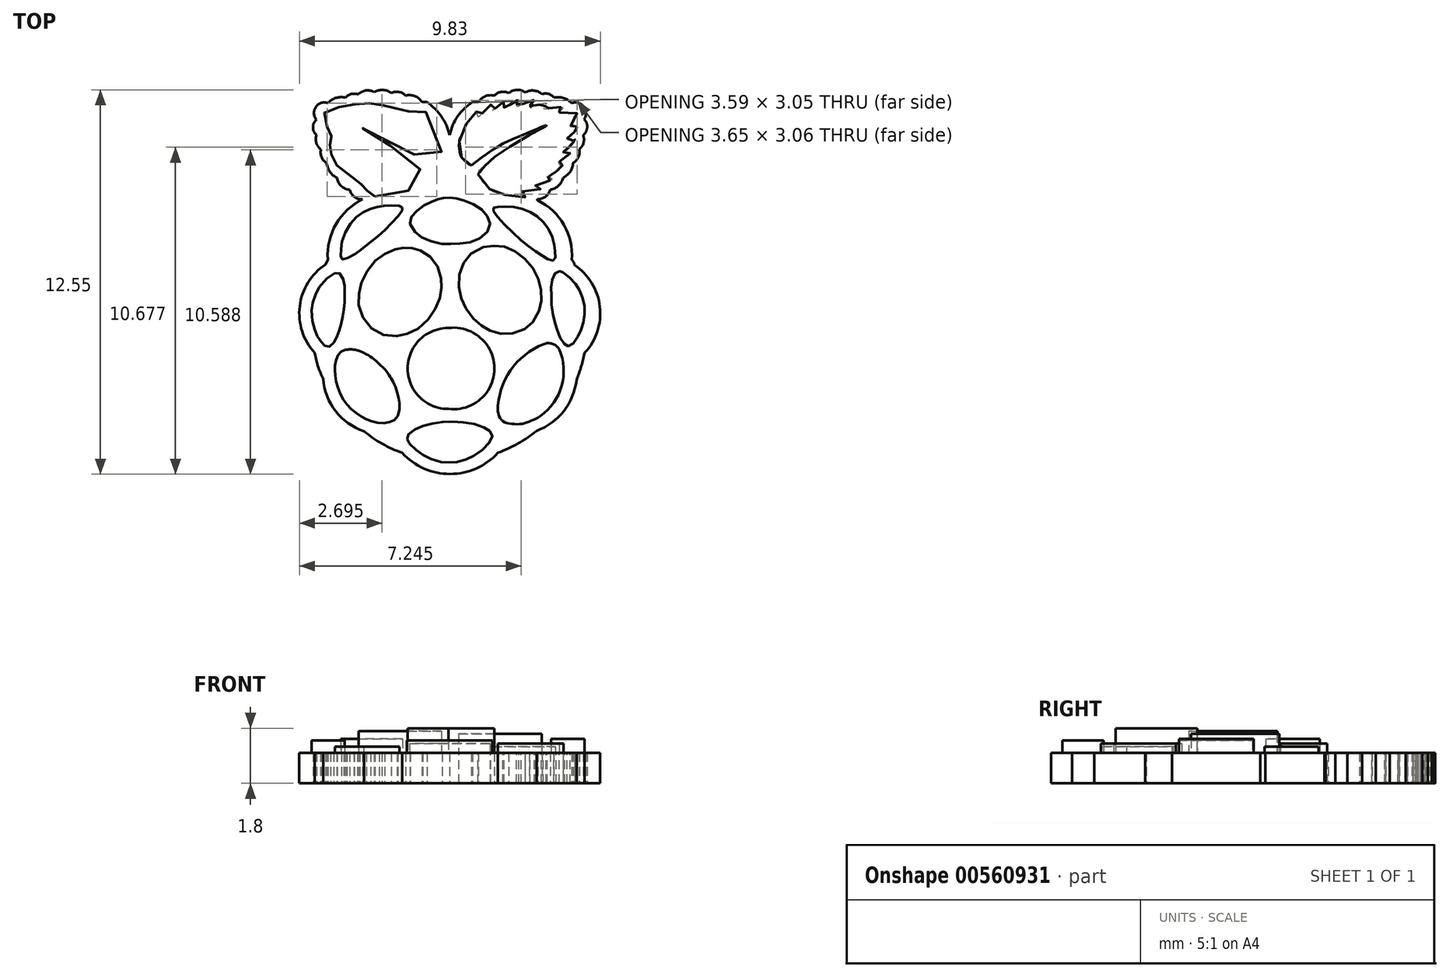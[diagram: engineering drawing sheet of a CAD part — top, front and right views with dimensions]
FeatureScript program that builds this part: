
annotation { "Feature Type Name" : "Feature", "Feature Type Description" : "" }
export const myFeature = defineFeature(function(context is Context, id is Id, definition is map)
    precondition{}
    {
        {
            var Q0;
            Q0=qCreatedBy(makeId("Top.planeOp"),FACE);
            var sketch = newSketch(context, id + "F0", { "sketchPlane" : qUnion([Q0])});
            skPoint(sketch, "E0", {"position": v(-4.99, 0) * mm});
            skArc(sketch, "E1", {"start": v(-2.8, 2.9) * mm, "mid": v(-3.67, 2.1) * mm, "end": v(-3.94, 0.95) * mm});
            skFitSpline(sketch, "E2", {"points": [v(-3.94, 0.95) * mm, v(-4.02, 0.78) * mm], "startDerivative": vector(-0.08, -0.17) * mm, "endDerivative": vector(-0.08, -0.17) * mm});
            skArc(sketch, "E3", {"start": v(-4.02, 0.78) * mm, "mid": v(-4.86, -0.59) * mm, "end": v(-4.37, -2.11) * mm});
            skArc(sketch, "E4", {"start": v(-4.37, -2.11) * mm, "mid": v(-4.26, -2.54) * mm, "end": v(-4.1, -2.96) * mm});
            skArc(sketch, "E5", {"start": v(-4.1, -2.96) * mm, "mid": v(-3.69, -4.01) * mm, "end": v(-2.76, -4.67) * mm});
            skArc(sketch, "E6", {"start": v(-2.76, -4.67) * mm, "mid": v(-2.17, -5.08) * mm, "end": v(-1.51, -5.37) * mm});
            skArc(sketch, "E7", {"start": v(-1.51, -5.37) * mm, "mid": v(0.05, -6.07) * mm, "end": v(1.6, -5.37) * mm});
            skArc(sketch, "E8", {"start": v(1.6, -5.37) * mm, "mid": v(2.27, -5.07) * mm, "end": v(2.88, -4.66) * mm});
            skArc(sketch, "E9", {"start": v(2.88, -4.66) * mm, "mid": v(3.76, -4) * mm, "end": v(4.18, -2.99) * mm});
            skArc(sketch, "E10", {"start": v(4.18, -2.99) * mm, "mid": v(4.33, -2.56) * mm, "end": v(4.45, -2.11) * mm});
            skArc(sketch, "E11", {"start": v(4.45, -2.11) * mm, "mid": v(4.94, -0.6) * mm, "end": v(4.11, 0.76) * mm});
            skArc(sketch, "E12", {"start": v(4.11, 0.76) * mm, "mid": v(4.09, 0.86) * mm, "end": v(4.03, 0.93) * mm});
            skArc(sketch, "E13", {"start": v(4.03, 0.93) * mm, "mid": v(3.77, 2.07) * mm, "end": v(2.92, 2.87) * mm});
            skArc(sketch, "E14", {"start": v(-3.23, 3.22) * mm, "mid": v(-3.07, 2.99) * mm, "end": v(-2.8, 2.9) * mm});
            skArc(sketch, "E15", {"start": v(-3.64, 3.6) * mm, "mid": v(-3.5, 3.34) * mm, "end": v(-3.23, 3.22) * mm});
            skArc(sketch, "E16", {"start": v(-3.98, 4.09) * mm, "mid": v(-3.87, 3.8) * mm, "end": v(-3.64, 3.6) * mm});
            skArc(sketch, "E17", {"start": v(-4.16, 4.53) * mm, "mid": v(-4.15, 4.28) * mm, "end": v(-3.98, 4.09) * mm});
            skArc(sketch, "E18", {"start": v(-4.31, 5) * mm, "mid": v(-4.31, 4.74) * mm, "end": v(-4.16, 4.53) * mm});
            skArc(sketch, "E19", {"start": v(-4.31, 5.5) * mm, "mid": v(-4.43, 5.26) * mm, "end": v(-4.31, 5) * mm});
            skArc(sketch, "E20", {"start": v(-3.94, 6.05) * mm, "mid": v(-4.33, 5.92) * mm, "end": v(-4.31, 5.5) * mm});
            skArc(sketch, "E21", {"start": v(-3.37, 6.23) * mm, "mid": v(-3.68, 6.22) * mm, "end": v(-3.94, 6.05) * mm});
            skArc(sketch, "E22", {"start": v(-2.95, 6.34) * mm, "mid": v(-3.17, 6.35) * mm, "end": v(-3.37, 6.23) * mm});
            skArc(sketch, "E23", {"start": v(-2.43, 6.4) * mm, "mid": v(-2.7, 6.46) * mm, "end": v(-2.95, 6.34) * mm});
            skArc(sketch, "E24", {"start": v(-1.87, 6.38) * mm, "mid": v(-2.15, 6.48) * mm, "end": v(-2.43, 6.4) * mm});
            skArc(sketch, "E25", {"start": v(-1.4, 6.3) * mm, "mid": v(-1.62, 6.41) * mm, "end": v(-1.87, 6.38) * mm});
            skArc(sketch, "E26", {"start": v(-0.87, 6.08) * mm, "mid": v(-1.1, 6.28) * mm, "end": v(-1.4, 6.3) * mm});
            skLineSegment(sketch, "E27", {"start": v(-0.87, 6.08) * mm, "end": v(-0.7, 6.08) * mm});
            skArc(sketch, "E28", {"start": v(0.04, 5) * mm, "mid": v(-0.24, 5.61) * mm, "end": v(-0.7, 6.08) * mm});
            skArc(sketch, "E29", {"start": v(0.79, 6.08) * mm, "mid": v(0.3, 5.62) * mm, "end": v(0.04, 5) * mm});
            skLineSegment(sketch, "E30", {"start": v(0.79, 6.08) * mm, "end": v(0.98, 6.08) * mm});
            skArc(sketch, "E31", {"start": v(1.5, 6.3) * mm, "mid": v(1.2, 6.27) * mm, "end": v(0.98, 6.08) * mm});
            skArc(sketch, "E32", {"start": v(1.97, 6.38) * mm, "mid": v(1.72, 6.41) * mm, "end": v(1.5, 6.3) * mm});
            skArc(sketch, "E33", {"start": v(2.5, 6.4) * mm, "mid": v(2.23, 6.48) * mm, "end": v(1.97, 6.38) * mm});
            skArc(sketch, "E34", {"start": v(3.05, 6.34) * mm, "mid": v(2.79, 6.46) * mm, "end": v(2.5, 6.4) * mm});
            skArc(sketch, "E35", {"start": v(3.44, 6.23) * mm, "mid": v(3.27, 6.35) * mm, "end": v(3.05, 6.34) * mm});
            skArc(sketch, "E36", {"start": v(4.02, 6.05) * mm, "mid": v(3.76, 6.21) * mm, "end": v(3.44, 6.23) * mm});
            skArc(sketch, "E37", {"start": v(4.43, 5.52) * mm, "mid": v(4.42, 5.93) * mm, "end": v(4.02, 6.05) * mm});
            skArc(sketch, "E38", {"start": v(4.4, 5) * mm, "mid": v(4.53, 5.26) * mm, "end": v(4.43, 5.52) * mm});
            skArc(sketch, "E39", {"start": v(4.27, 4.54) * mm, "mid": v(4.4, 4.75) * mm, "end": v(4.4, 5) * mm});
            skArc(sketch, "E40", {"start": v(4.07, 4.1) * mm, "mid": v(4.24, 4.28) * mm, "end": v(4.27, 4.54) * mm});
            skArc(sketch, "E41", {"start": v(3.74, 3.6) * mm, "mid": v(3.97, 3.8) * mm, "end": v(4.07, 4.1) * mm});
            skArc(sketch, "E42", {"start": v(3.33, 3.23) * mm, "mid": v(3.6, 3.35) * mm, "end": v(3.74, 3.6) * mm});
            skArc(sketch, "E43", {"start": v(2.9, 2.9) * mm, "mid": v(3.17, 3) * mm, "end": v(3.33, 3.23) * mm});
            skFitSpline(sketch, "E44", {"points": [v(2.9, 2.9) * mm, v(2.9, 2.9) * mm, v(2.9, 2.88) * mm, v(2.92, 2.87) * mm], "startDerivative": vector(-0.04, -0.02) * mm, "endDerivative": vector(0.06, -0.02) * mm});
            skFitSpline(sketch, "E45", {"points": [v(-1.35, -4.93) * mm, v(-1.36, -4.9) * mm, v(-1.31, -4.78) * mm, v(-1.15, -4.63) * mm, v(-0.91, -4.53) * mm, v(-0.63, -4.44) * mm, v(-0.28, -4.37) * mm, v(0.05, -4.36) * mm, v(0.44, -4.37) * mm, v(0.85, -4.44) * mm, v(1.17, -4.55) * mm, v(1.3, -4.64) * mm, v(1.4, -4.72) * mm, v(1.43, -4.83) * mm, v(1.38, -4.96) * mm, v(1.2, -5.2) * mm, v(0.87, -5.44) * mm, v(0.68, -5.54) * mm, v(0.41, -5.65) * mm, v(0.14, -5.68) * mm, v(-0.01, -5.7) * mm, v(-0.28, -5.67) * mm, v(-0.63, -5.55) * mm, v(-0.83, -5.44) * mm, v(-1.03, -5.3) * mm, v(-1.25, -5.1) * mm, v(-1.32, -5) * mm, v(-1.35, -4.93) * mm]});
            skArc(sketch, "E46", {"start": v(0, -1.3) * mm, "mid": v(-1.33, -2.62) * mm, "end": v(0, -3.94) * mm});
            skArc(sketch, "E47", {"start": v(0, -3.94) * mm, "mid": v(1.5, -2.62) * mm, "end": v(0, -1.3) * mm});
            skLineSegment(sketch, "E48", {"start": v(0.05, -3.96) * mm, "end": v(0.05, -4.44) * mm, "construction": true});
            skLineSegment(sketch, "E49", {"start": v(-4.7, 0) * mm, "end": v(-4.99, 0) * mm, "construction": true});
            skLineSegment(sketch, "E50", {"start": v(0.04, 5) * mm, "end": v(0.05, 6.52) * mm, "construction": true});
            skFitSpline(sketch, "E51", {"points": [v(-3.5, -2.07) * mm, v(-3.4, -2.02) * mm, v(-3.26, -2) * mm, v(-3.14, -2) * mm, v(-3, -2.02) * mm, v(-2.88, -2.06) * mm, v(-2.77, -2.11) * mm], "startDerivative": vector(0.63, 0.36) * mm, "endDerivative": vector(0.7, -0.31) * mm});
            skFitSpline(sketch, "E52", {"points": [v(-2.77, -2.11) * mm, v(-2.6, -2.2) * mm, v(-2.46, -2.3) * mm, v(-2.3, -2.44) * mm, v(-2.05, -2.69) * mm, v(-1.92, -2.88) * mm, v(-1.86, -2.95) * mm, v(-1.78, -3.12) * mm, v(-1.7, -3.34) * mm, v(-1.64, -3.53) * mm, v(-1.62, -3.6) * mm], "startDerivative": vector(2.02, -1.01) * mm, "endDerivative": vector(0.5, -0.89) * mm});
            skFitSpline(sketch, "E53", {"points": [v(-1.62, -3.6) * mm, v(-1.6, -3.74) * mm, v(-1.6, -3.98) * mm, v(-1.7, -4.24) * mm, v(-1.83, -4.34) * mm, v(-2.03, -4.4) * mm, v(-2.27, -4.4) * mm, v(-2.54, -4.34) * mm, v(-2.7, -4.27) * mm, v(-2.9, -4.16) * mm, v(-3.1, -4) * mm, v(-3.3, -3.82) * mm, v(-3.43, -3.64) * mm, v(-3.56, -3.38) * mm, v(-3.66, -3.1) * mm, v(-3.7, -2.84) * mm, v(-3.71, -2.68) * mm, v(-3.71, -2.54) * mm, v(-3.67, -2.33) * mm, v(-3.6, -2.16) * mm, v(-3.5, -2.07) * mm], "startDerivative": vector(0.52, -3.3) * mm, "endDerivative": vector(2.4, 2.14) * mm});
            skArc(sketch, "E54", {"start": v(3.1, -1.82) * mm, "mid": v(2.02, -2.69) * mm, "end": v(1.6, -4.02) * mm});
            skArc(sketch, "E55", {"start": v(3.61, -1.99) * mm, "mid": v(3.4, -1.81) * mm, "end": v(3.1, -1.82) * mm});
            skArc(sketch, "E56", {"start": v(3, -4.17) * mm, "mid": v(3.7, -3.2) * mm, "end": v(3.61, -1.99) * mm});
            skFitSpline(sketch, "E57", {"points": [v(1.6, -4.02) * mm, v(1.64, -4.14) * mm, v(1.76, -4.33) * mm, v(2, -4.42) * mm, v(2.34, -4.44) * mm, v(2.65, -4.35) * mm, v(2.9, -4.23) * mm, v(3, -4.17) * mm], "startDerivative": vector(0.21, -1.07) * mm, "endDerivative": vector(0.8, 0.56) * mm});
            skFitSpline(sketch, "E58", {"points": [v(-1.47, 1.32) * mm, v(-1.57, 1.32) * mm, v(-1.9, 1.22) * mm, v(-2.17, 1.07) * mm, v(-2.48, 0.8) * mm, v(-2.75, 0.4) * mm, v(-2.9, 0.04) * mm, v(-2.94, -0.27) * mm, v(-2.92, -0.62) * mm, v(-2.73, -1.06) * mm, v(-2.37, -1.41) * mm, v(-1.88, -1.56) * mm, v(-1.51, -1.54) * mm, v(-1.22, -1.44) * mm, v(-0.84, -1.2) * mm, v(-0.52, -0.82) * mm, v(-0.35, -0.51) * mm, v(-0.24, -0.16) * mm, v(-0.23, 0.08) * mm, v(-0.24, 0.3) * mm, v(-0.35, 0.7) * mm, v(-0.58, 1) * mm, v(-0.87, 1.21) * mm, v(-1.08, 1.28) * mm, v(-1.27, 1.32) * mm, v(-1.47, 1.32) * mm]});
            skFitSpline(sketch, "E59", {"points": [v(1.49, 1.4) * mm, v(1.62, 1.39) * mm, v(1.8, 1.36) * mm, v(1.95, 1.3) * mm, v(2.18, 1.2) * mm, v(2.35, 1.09) * mm, v(2.56, 0.9) * mm, v(2.7, 0.73) * mm, v(2.82, 0.55) * mm, v(2.92, 0.34) * mm, v(3, 0.1) * mm, v(3.02, -0.05) * mm, v(3.04, -0.2) * mm, v(3.03, -0.42) * mm, v(3, -0.56) * mm, v(2.95, -0.75) * mm, v(2.83, -1) * mm, v(2.7, -1.16) * mm, v(2.59, -1.26) * mm, v(2.39, -1.38) * mm, v(2.14, -1.47) * mm, v(1.96, -1.49) * mm, v(1.71, -1.48) * mm, v(1.5, -1.43) * mm, v(1.34, -1.37) * mm, v(1.2, -1.3) * mm, v(1.08, -1.22) * mm, v(0.93, -1.1) * mm, v(0.8, -0.97) * mm, v(0.65, -0.8) * mm, v(0.52, -0.58) * mm, v(0.44, -0.42) * mm, v(0.4, -0.24) * mm, v(0.36, -0.06) * mm, v(0.33, 0.19) * mm, v(0.35, 0.43) * mm, v(0.4, 0.65) * mm, v(0.52, 0.88) * mm, v(0.63, 1.03) * mm, v(0.86, 1.22) * mm, v(1.13, 1.34) * mm, v(1.35, 1.39) * mm, v(1.49, 1.4) * mm]});
            skFitSpline(sketch, "E60", {"points": [v(3.63, 0.56) * mm, v(3.5, 0.52) * mm, v(3.41, 0.35) * mm, v(3.36, 0.06) * mm, v(3.36, -0.27) * mm, v(3.39, -0.72) * mm, v(3.5, -1.16) * mm, v(3.53, -1.27) * mm, v(3.64, -1.6) * mm, v(3.8, -1.83) * mm, v(3.88, -1.88) * mm, v(3.98, -1.88) * mm, v(4.17, -1.67) * mm, v(4.3, -1.42) * mm, v(4.4, -1.15) * mm, v(4.44, -0.82) * mm, v(4.43, -0.5) * mm, v(4.32, -0.16) * mm, v(4.19, 0.09) * mm, v(3.95, 0.36) * mm, v(3.7, 0.54) * mm, v(3.66, 0.55) * mm, v(3.63, 0.56) * mm]});
            skFitSpline(sketch, "E61", {"points": [v(-3.72, 0.5) * mm, v(-3.7, 0.51) * mm, v(-3.61, 0.52) * mm, v(-3.57, 0.5) * mm, v(-3.52, 0.46) * mm, v(-3.48, 0.4) * mm, v(-3.43, 0.27) * mm, v(-3.42, 0.18) * mm, v(-3.4, 0.07) * mm, v(-3.39, -0.06) * mm, v(-3.39, -0.17) * mm, v(-3.4, -0.35) * mm, v(-3.4, -0.47) * mm, v(-3.4, -0.59) * mm, v(-3.42, -0.66) * mm, v(-3.44, -0.82) * mm, v(-3.46, -0.91) * mm, v(-3.47, -0.98) * mm, v(-3.5, -1.1) * mm, v(-3.52, -1.22) * mm, v(-3.54, -1.3) * mm, v(-3.58, -1.4) * mm, v(-3.6, -1.5) * mm, v(-3.64, -1.56) * mm, v(-3.67, -1.64) * mm, v(-3.72, -1.72) * mm, v(-3.77, -1.8) * mm, v(-3.83, -1.87) * mm, v(-3.87, -1.9) * mm, v(-3.9, -1.91) * mm, v(-3.98, -1.91) * mm, v(-4.01, -1.9) * mm, v(-4.04, -1.88) * mm, v(-4.07, -1.85) * mm, v(-4.1, -1.82) * mm, v(-4.15, -1.76) * mm, v(-4.2, -1.7) * mm, v(-4.26, -1.6) * mm, v(-4.3, -1.51) * mm, v(-4.35, -1.4) * mm, v(-4.4, -1.3) * mm, v(-4.44, -1.13) * mm, v(-4.47, -0.91) * mm, v(-4.47, -0.72) * mm, v(-4.46, -0.63) * mm, v(-4.44, -0.47) * mm, v(-4.42, -0.4) * mm, v(-4.35, -0.21) * mm, v(-4.3, -0.12) * mm, v(-4.22, 0.05) * mm, v(-4.03, 0.27) * mm, v(-3.84, 0.42) * mm, v(-3.72, 0.5) * mm]});
            skFitSpline(sketch, "E62", {"points": [v(-1.5, 2.65) * mm, v(-1.53, 2.68) * mm, v(-1.67, 2.7) * mm, v(-1.97, 2.7) * mm, v(-2.23, 2.68) * mm, v(-2.5, 2.61) * mm, v(-2.8, 2.48) * mm, v(-3.05, 2.28) * mm, v(-3.33, 1.92) * mm, v(-3.5, 1.46) * mm, v(-3.51, 1.21) * mm, v(-3.52, 1) * mm, v(-3.47, 0.95) * mm, v(-3.36, 0.96) * mm, v(-3.07, 1.12) * mm, v(-2.85, 1.27) * mm, v(-2.33, 1.68) * mm, v(-2, 1.98) * mm, v(-1.67, 2.34) * mm, v(-1.52, 2.55) * mm, v(-1.5, 2.6) * mm, v(-1.5, 2.65) * mm]});
            skFitSpline(sketch, "E63", {"points": [v(-0.35, 2.9) * mm, v(-0.58, 2.82) * mm, v(-0.9, 2.65) * mm, v(-1.16, 2.4) * mm, v(-1.27, 2.19) * mm, v(-1.08, 1.82) * mm, v(-0.75, 1.6) * mm, v(-0.18, 1.44) * mm, v(0.2, 1.46) * mm, v(0.69, 1.5) * mm, v(1.16, 1.73) * mm, v(1.36, 2.08) * mm, v(1.26, 2.37) * mm, v(0.98, 2.65) * mm, v(0.48, 2.88) * mm, v(0.22, 2.94) * mm, v(0.03, 2.96) * mm, v(-0.2, 2.94) * mm, v(-0.35, 2.9) * mm]});
            skFitSpline(sketch, "E64", {"points": [v(1.47, 2.63) * mm, v(1.45, 2.56) * mm, v(1.61, 2.32) * mm, v(2.24, 1.68) * mm, v(2.75, 1.27) * mm, v(3.11, 1.03) * mm, v(3.34, 0.91) * mm, v(3.48, 0.93) * mm, v(3.48, 1.18) * mm, v(3.45, 1.48) * mm, v(3.26, 1.96) * mm, v(2.91, 2.33) * mm, v(2.5, 2.56) * mm, v(1.97, 2.67) * mm, v(1.58, 2.66) * mm, v(1.47, 2.63) * mm]});
            skFitSpline(sketch, "E65", {"points": [v(-2.4, 3) * mm, v(-2.32, 2.99) * mm, v(-2.04, 3) * mm, v(-1.73, 3.04) * mm, v(-1.5, 3.1) * mm, v(-1.28, 3.2) * mm, v(-1.09, 3.36) * mm, v(-0.96, 3.5) * mm, v(-0.9, 3.62) * mm, v(-0.84, 3.77) * mm, v(-0.84, 3.78) * mm, v(-0.9, 3.86) * mm, v(-1.03, 3.99) * mm, v(-1.21, 4.14) * mm, v(-1.4, 4.29) * mm, v(-1.61, 4.43) * mm, v(-2.23, 4.88) * mm, v(-2.92, 5.22) * mm, v(-3.08, 5.3) * mm, v(-3.05, 5.3) * mm, v(-2.44, 5.08) * mm, v(-1.76, 4.76) * mm, v(-1.33, 4.5) * mm, v(-0.86, 4.2) * mm, v(-0.64, 4) * mm, v(-0.56, 4.05) * mm, v(-0.35, 4.22) * mm, v(-0.22, 4.48) * mm, v(-0.23, 4.84) * mm, v(-0.36, 5.18) * mm, v(-0.6, 5.57) * mm, v(-0.77, 5.75) * mm, v(-0.83, 5.59) * mm, v(-1, 5.76) * mm, v(-1.25, 6) * mm, v(-1.25, 5.88) * mm, v(-1.31, 5.78) * mm, v(-1.43, 5.91) * mm, v(-1.55, 6.01) * mm, v(-1.67, 6.08) * mm, v(-1.66, 6.04) * mm, v(-1.65, 6) * mm, v(-1.7, 5.9) * mm, v(-1.72, 5.87) * mm, v(-1.8, 5.94) * mm, v(-1.93, 6.04) * mm, v(-2.1, 6.13) * mm, v(-2.18, 6.16) * mm, v(-2.16, 6.13) * mm, v(-2.11, 6.06) * mm, v(-2.1, 6.01) * mm, v(-2.1, 5.96) * mm, v(-2.14, 5.93) * mm, v(-2.2, 5.97) * mm, v(-2.3, 6.03) * mm, v(-2.45, 6.09) * mm, v(-2.65, 6.14) * mm, v(-2.69, 6.14) * mm, v(-2.63, 6.08) * mm, v(-2.55, 6.01) * mm, v(-2.55, 5.96) * mm, v(-2.57, 5.92) * mm, v(-2.74, 5.98) * mm, v(-2.92, 6.01) * mm, v(-3.05, 6.04) * mm, v(-3.1, 6.05) * mm, v(-3.05, 6) * mm, v(-3, 5.94) * mm, v(-2.98, 5.89) * mm, v(-3, 5.85) * mm, v(-3.01, 5.84) * mm, v(-3.19, 5.89) * mm, v(-3.34, 5.92) * mm, v(-3.5, 5.92) * mm, v(-3.64, 5.9) * mm, v(-3.6, 5.85) * mm, v(-3.52, 5.78) * mm, v(-3.5, 5.74) * mm, v(-3.65, 5.74) * mm, v(-3.94, 5.73) * mm, v(-4.06, 5.73) * mm, v(-4.07, 5.73) * mm, v(-4.06, 5.7) * mm, v(-4.02, 5.64) * mm, v(-3.97, 5.57) * mm, v(-3.9, 5.44) * mm, v(-3.87, 5.34) * mm, v(-3.86, 5.28) * mm, v(-3.89, 5.27) * mm, v(-3.94, 5.27) * mm, v(-4.03, 5.27) * mm, v(-4.1, 5.28) * mm, v(-4.1, 5.28) * mm, v(-4.1, 5.26) * mm, v(-4.1, 5.26) * mm, v(-4.09, 5.25) * mm, v(-4.06, 5.2) * mm, v(-4.05, 5.18) * mm, v(-4.03, 5.16) * mm, v(-4.01, 5.13) * mm, v(-4, 5.11) * mm, v(-3.97, 5.1) * mm, v(-3.8, 4.93) * mm, v(-3.76, 4.9) * mm, v(-3.76, 4.87) * mm, v(-3.8, 4.85) * mm, v(-3.89, 4.84) * mm, v(-3.98, 4.86) * mm, v(-4.01, 4.87) * mm, v(-3.98, 4.8) * mm, v(-3.93, 4.73) * mm, v(-3.82, 4.63) * mm, v(-3.72, 4.53) * mm, v(-3.67, 4.47) * mm, v(-3.63, 4.45) * mm, v(-3.67, 4.43) * mm, v(-3.72, 4.42) * mm, v(-3.8, 4.42) * mm, v(-3.85, 4.43) * mm, v(-3.85, 4.4) * mm, v(-3.81, 4.36) * mm, v(-3.65, 4.22) * mm, v(-3.53, 4.13) * mm, v(-3.41, 4.06) * mm, v(-3.44, 4.04) * mm, v(-3.51, 4.02) * mm, v(-3.59, 4.02) * mm, v(-3.65, 4.02) * mm, v(-3.6, 3.98) * mm, v(-3.5, 3.9) * mm, v(-3.39, 3.83) * mm, v(-3.25, 3.75) * mm, v(-3.15, 3.7) * mm, v(-3.1, 3.67) * mm, v(-3.13, 3.65) * mm, v(-3.17, 3.63) * mm, v(-3.24, 3.62) * mm, v(-3.32, 3.62) * mm, v(-3.3, 3.6) * mm, v(-3.22, 3.54) * mm, v(-3.12, 3.5) * mm, v(-3.02, 3.47) * mm, v(-2.9, 3.43) * mm, v(-2.81, 3.4) * mm, v(-2.74, 3.38) * mm, v(-2.76, 3.34) * mm, v(-2.8, 3.3) * mm, v(-2.88, 3.28) * mm, v(-2.9, 3.27) * mm, v(-2.88, 3.25) * mm, v(-2.82, 3.23) * mm, v(-2.76, 3.21) * mm, v(-2.68, 3.2) * mm, v(-2.6, 3.19) * mm, v(-2.53, 3.18) * mm, v(-2.44, 3.17) * mm, v(-2.34, 3.17) * mm, v(-2.28, 3.15) * mm, v(-2.26, 3.13) * mm, v(-2.3, 3.07) * mm, v(-2.33, 3.04) * mm, v(-2.4, 3) * mm]});
            skFitSpline(sketch, "E66", {"points": [v(0.75, 4.01) * mm, v(1.76, 4.71) * mm, v(2.82, 5.17) * mm, v(3.18, 5.32) * mm, v(3.2, 5.32) * mm, v(3.12, 5.26) * mm, v(2.87, 5.13) * mm, v(2.64, 5) * mm], "startDerivative": vector(3.75, 2.92) * mm, "endDerivative": vector(-1.9, -1.01) * mm});
            skFitSpline(sketch, "E67", {"points": [v(2.64, 5) * mm, v(1.78, 4.49) * mm, v(1.37, 4.17) * mm, v(1.14, 3.97) * mm, v(0.96, 3.78) * mm, v(1.34, 3.24) * mm, v(1.88, 3.04) * mm, v(2.5, 2.99) * mm, v(2.37, 3.13) * mm, v(2.9, 3.21) * mm, v(3.03, 3.28) * mm, v(2.84, 3.35) * mm, v(3.16, 3.47) * mm, v(3.43, 3.62) * mm, v(3.19, 3.65) * mm, v(3.61, 3.86) * mm, v(3.78, 4) * mm, v(3.52, 4.04) * mm, v(3.8, 4.25) * mm, v(3.97, 4.41) * mm, v(3.95, 4.41) * mm, v(3.8, 4.42) * mm, v(3.75, 4.45) * mm, v(3.8, 4.5) * mm, v(3.9, 4.58) * mm, v(4, 4.68) * mm, v(4.1, 4.8) * mm, v(4.13, 4.87) * mm, v(4.1, 4.86) * mm, v(3.98, 4.84) * mm, v(3.9, 4.85) * mm, v(3.87, 4.88) * mm, v(3.94, 4.96) * mm, v(4.09, 5.09) * mm, v(4.2, 5.22) * mm, v(4.22, 5.28) * mm, v(4.2, 5.28) * mm], "startDerivative": vector(-15.35, -9.04) * mm, "endDerivative": vector(-2.79, -1.04) * mm});
            skFitSpline(sketch, "E68", {"points": [v(4.2, 5.28) * mm, v(4.13, 5.27) * mm, v(4.03, 5.27) * mm, v(4, 5.27) * mm, v(3.98, 5.28) * mm, v(3.98, 5.3) * mm, v(3.99, 5.31) * mm, v(4, 5.39) * mm, v(4.07, 5.53) * mm, v(4.1, 5.6) * mm, v(4.2, 5.72) * mm, v(4.2, 5.73) * mm, v(3.88, 5.73) * mm, v(3.62, 5.74) * mm, v(3.63, 5.76) * mm, v(3.71, 5.84) * mm, v(3.76, 5.9) * mm, v(3.75, 5.9) * mm, v(3.7, 5.91) * mm, v(3.63, 5.92) * mm, v(3.53, 5.92) * mm, v(3.46, 5.91) * mm, v(3.33, 5.9) * mm, v(3.24, 5.87) * mm, v(3.16, 5.85) * mm, v(3.13, 5.84) * mm, v(3.11, 5.85) * mm, v(3.1, 5.9) * mm, v(3.13, 5.96) * mm, v(3.22, 6.04) * mm, v(3.2, 6.05) * mm, v(3.17, 6.04) * mm, v(3.07, 6.02) * mm, v(2.9, 5.98) * mm, v(2.8, 5.95) * mm, v(2.71, 5.92) * mm, v(2.69, 5.92) * mm, v(2.68, 5.93) * mm, v(2.67, 5.95) * mm, v(2.67, 6) * mm, v(2.7, 6.04) * mm, v(2.75, 6.09) * mm, v(2.8, 6.13) * mm, v(2.8, 6.14) * mm, v(2.79, 6.14) * mm, v(2.73, 6.13) * mm, v(2.6, 6.1) * mm, v(2.5, 6.06) * mm, v(2.44, 6.03) * mm, v(2.36, 5.99) * mm, v(2.3, 5.95) * mm, v(2.27, 5.93) * mm, v(2.25, 5.94) * mm, v(2.22, 5.98) * mm, v(2.22, 6.02) * mm, v(2.22, 6.05) * mm, v(2.26, 6.1) * mm, v(2.3, 6.14) * mm, v(2.3, 6.15) * mm, v(2.3, 6.16) * mm, v(2.28, 6.16) * mm, v(2.26, 6.15) * mm, v(2.22, 6.13) * mm, v(2.17, 6.1) * mm, v(2.12, 6.08) * mm, v(2.09, 6.06) * mm, v(2.04, 6.03) * mm, v(2, 6) * mm, v(1.96, 5.96) * mm, v(1.92, 5.93) * mm, v(1.89, 5.9) * mm, v(1.86, 5.88) * mm, v(1.85, 5.88) * mm, v(1.82, 5.9) * mm, v(1.8, 5.93) * mm, v(1.78, 5.95) * mm, v(1.78, 5.98) * mm, v(1.78, 6) * mm, v(1.78, 6.03) * mm, v(1.8, 6.07) * mm, v(1.82, 6.1) * mm, v(1.8, 6.1) * mm, v(1.8, 6.09) * mm, v(1.76, 6.07) * mm, v(1.72, 6.04) * mm, v(1.67, 6) * mm, v(1.5, 5.84) * mm, v(1.44, 5.77) * mm, v(1.4, 5.81) * mm, v(1.37, 5.86) * mm, v(1.38, 6) * mm, v(1.35, 5.98) * mm, v(1.27, 5.9) * mm, v(1.18, 5.8) * mm, v(1.1, 5.72) * mm, v(1, 5.6) * mm, v(0.98, 5.59) * mm, v(0.94, 5.63) * mm, v(0.92, 5.74) * mm, v(0.9, 5.76) * mm, v(0.84, 5.7) * mm, v(0.7, 5.54) * mm, v(0.58, 5.36) * mm, v(0.48, 5.18) * mm, v(0.4, 4.96) * mm, v(0.34, 4.66) * mm, v(0.36, 4.52) * mm, v(0.4, 4.31) * mm, v(0.52, 4.18) * mm, v(0.6, 4.1) * mm, v(0.68, 4.05) * mm, v(0.75, 4.01) * mm], "startDerivative": vector(-6.74, -0.46) * mm, "endDerivative": vector(6.78, -3.17) * mm});
            skSolve(sketch);
        }
        {
            var Q0;
            Q0 = qSketchRegion(id + "F0", true);
            extrude(context, id + "F1", {"entities" : qUnion([Q0]), "depth" : 1 * mm, "offsetDistance" : 25 * mm});
        }
        {
            var Q0;
            Q0=makeQuery(id+"F0.imprint","IMPRINT",FACE,{"disambiguationData":[TD([[makeQuery(id+"F0.imprint","IMPRINT",EDGE,{"derivedFrom":sQuery(id+"F0.wireOp",EDGE,"E64")}),1.0]])]});
            var Q1;
            Q1=makeQuery(id+"F0.imprint","IMPRINT",FACE,{"disambiguationData":[TD([[makeQuery(id+"F0.imprint","IMPRINT",EDGE,{"derivedFrom":sQuery(id+"F0.wireOp",EDGE,"E51")}),-1.0]])]});
            extrude(context, id + "F2", {"entities" : qUnion([Q0, Q1]), "operationType" : NewBodyOperationType.ADD, "depth" : 1.2 * mm, "offsetDistance" : 25 * mm});
        }
        {
            var Q0;
            Q0=makeQuery(id+"F0.imprint","IMPRINT",FACE,{"disambiguationData":[TD([[makeQuery(id+"F0.imprint","IMPRINT",EDGE,{"derivedFrom":sQuery(id+"F0.wireOp",EDGE,"E54")}),1.0]])]});
            var Q1;
            Q1=makeQuery(id+"F0.imprint","IMPRINT",FACE,{"disambiguationData":[TD([[makeQuery(id+"F0.imprint","IMPRINT",EDGE,{"derivedFrom":sQuery(id+"F0.wireOp",EDGE,"E63")}),1.0]])]});
            extrude(context, id + "F3", {"entities" : qUnion([Q0, Q1]), "operationType" : NewBodyOperationType.ADD, "depth" : 1.3 * mm, "offsetDistance" : 25 * mm});
        }
        {
            var Q0;
            Q0=makeQuery(id+"F0.imprint","IMPRINT",FACE,{"disambiguationData":[TD([[makeQuery(id+"F0.imprint","IMPRINT",EDGE,{"derivedFrom":sQuery(id+"F0.wireOp",EDGE,"E61")}),-1.0]])]});
            var Q1;
            Q1=makeQuery(id+"F0.imprint","IMPRINT",FACE,{"disambiguationData":[TD([[makeQuery(id+"F0.imprint","IMPRINT",EDGE,{"derivedFrom":sQuery(id+"F0.wireOp",EDGE,"E45")}),-1.0]])]});
            extrude(context, id + "F4", {"entities" : qUnion([Q0, Q1]), "operationType" : NewBodyOperationType.ADD, "depth" : 1.4 * mm, "offsetDistance" : 25 * mm});
        }
        {
            var Q0;
            Q0=makeQuery(id+"F0.imprint","IMPRINT",FACE,{"disambiguationData":[TD([[makeQuery(id+"F0.imprint","IMPRINT",EDGE,{"derivedFrom":sQuery(id+"F0.wireOp",EDGE,"E60")}),1.0]])]});
            var Q1;
            Q1=makeQuery(id+"F0.imprint","IMPRINT",FACE,{"disambiguationData":[TD([[makeQuery(id+"F0.imprint","IMPRINT",EDGE,{"derivedFrom":sQuery(id+"F0.wireOp",EDGE,"E62")}),1.0]])]});
            extrude(context, id + "F5", {"entities" : qUnion([Q0, Q1]), "operationType" : NewBodyOperationType.ADD, "depth" : 1.45 * mm, "offsetDistance" : 25 * mm});
        }
        {
            var Q0;
            Q0=makeQuery(id+"F0.imprint","IMPRINT",FACE,{"disambiguationData":[TD([[makeQuery(id+"F0.imprint","IMPRINT",EDGE,{"derivedFrom":sQuery(id+"F0.wireOp",EDGE,"E58")}),1.0]])]});
            extrude(context, id + "F6", {"entities" : qUnion([Q0]), "operationType" : NewBodyOperationType.ADD, "depth" : 1.71 * mm, "offsetDistance" : 25 * mm});
        }
        {
            var Q0;
            Q0=makeQuery(id+"F0.imprint","IMPRINT",FACE,{"disambiguationData":[TD([[makeQuery(id+"F0.imprint","IMPRINT",EDGE,{"derivedFrom":sQuery(id+"F0.wireOp",EDGE,"E46")}),1.0]])]});
            extrude(context, id + "F7", {"entities" : qUnion([Q0]), "operationType" : NewBodyOperationType.ADD, "depth" : 1.8 * mm, "offsetDistance" : 25 * mm});
        }
        {
            var Q0;
            Q0=makeQuery(id+"F0.imprint","IMPRINT",FACE,{"disambiguationData":[TD([[makeQuery(id+"F0.imprint","IMPRINT",EDGE,{"derivedFrom":sQuery(id+"F0.wireOp",EDGE,"E59")}),-1.0]])]});
            extrude(context, id + "F8", {"entities" : qUnion([Q0]), "operationType" : NewBodyOperationType.ADD, "depth" : 1.62 * mm, "offsetDistance" : 25 * mm});
        }
    });
